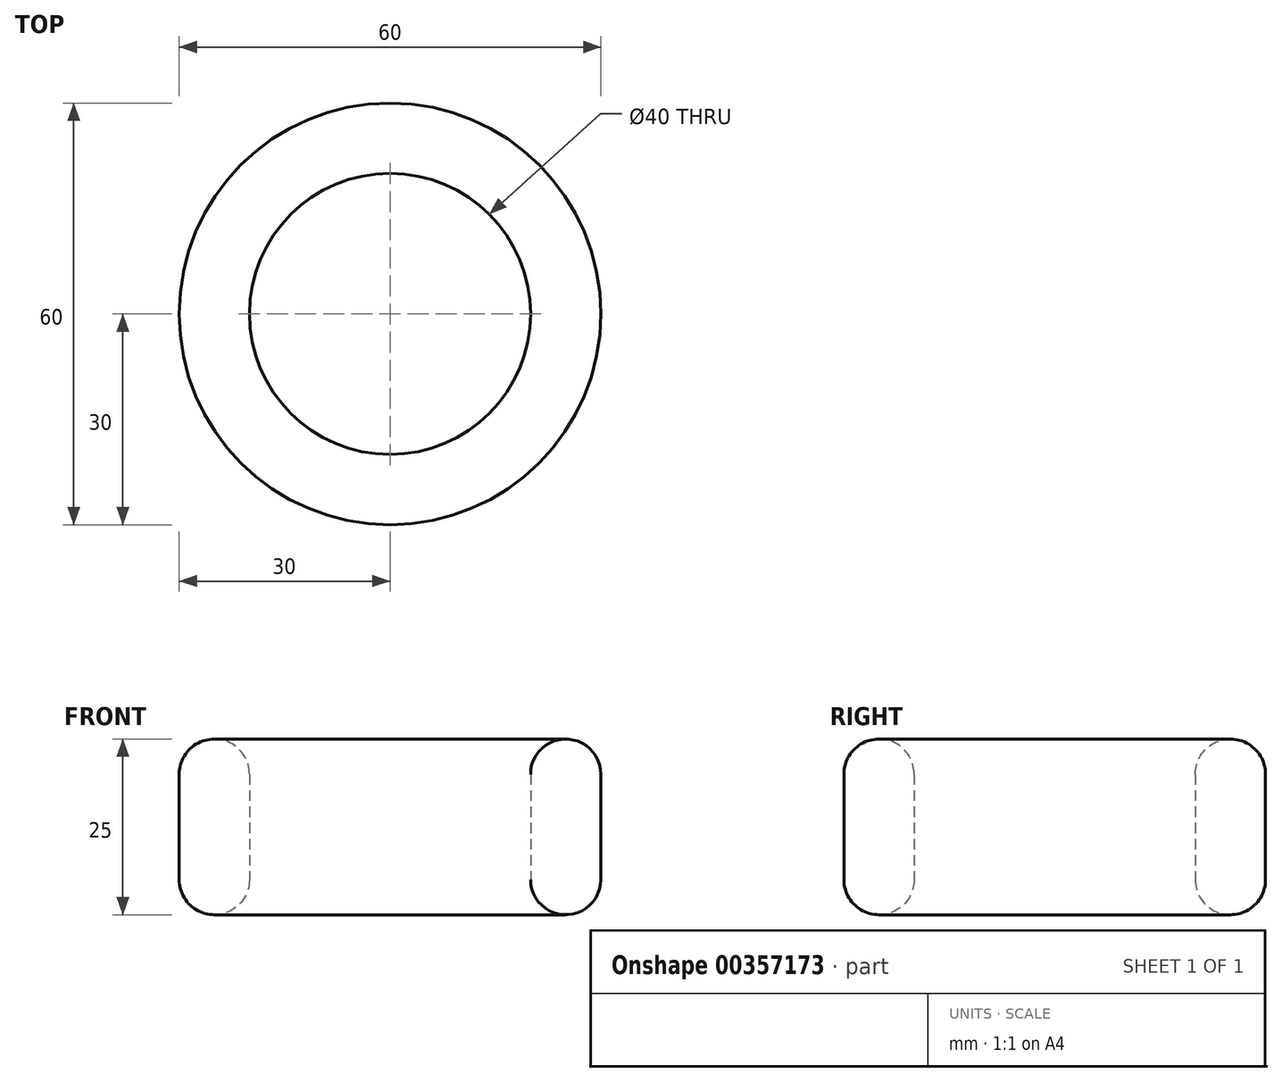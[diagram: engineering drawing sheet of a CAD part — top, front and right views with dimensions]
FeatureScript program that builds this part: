
annotation { "Feature Type Name" : "Feature", "Feature Type Description" : "" }
export const myFeature = defineFeature(function(context is Context, id is Id, definition is map)
    precondition{}
    {
        {
            var Q0;
            Q0=qCreatedBy(makeId("Top.planeOp"),FACE);
            var sketch = newSketch(context, id + "F0", { "sketchPlane" : qUnion([Q0])});
            skCircle(sketch, "E0", {"center": v(0, 0) * mm, "radius": 30 * mm});
            skCircle(sketch, "E1", {"center": v(0, 0) * mm, "radius": 20 * mm});
            skCircle(sketch, "E2", {"center": v(0, 0) * mm, "radius": 7.5 * mm});
            skSolve(sketch);
        }
        {
            var Q0;
            Q0 = qSketchRegion(id + "F0", true);
            extrude(context, id + "F1", {"entities" : qUnion([Q0]), "depth" : 25 * mm});
        }
        {
            var Q0;
            Q0=makeQuery(id+"F1.opExtrude","CAP_EDGE",EDGE,{"disambiguationData":[OSD([sQuery(id+"F0.wireOp",EDGE,"E0")])],"isStart":false});
            var Q1;
            Q1=makeQuery(id+"F1.opExtrude","CAP_FACE",FACE,{"disambiguationData":[OSD([sQuery(id+"F0.wireOp",EDGE,"E0"),sQuery(id+"F0.wireOp",EDGE,"E1")])],"isStart":false});
            var Q2;
            Q2=makeQuery(id+"F1.opExtrude","SWEPT_FACE",FACE,{"disambiguationData":[OSD([sQuery(id+"F0.wireOp",EDGE,"E0")])]});
            var Q3;
            Q3=makeQuery(id+"F1.opExtrude","CAP_FACE",FACE,{"disambiguationData":[OSD([sQuery(id+"F0.wireOp",EDGE,"E0"),sQuery(id+"F0.wireOp",EDGE,"E1")])],"isStart":true});
            fillet(context, id + "F2", {"entities" : qUnion([Q0, Q1, Q2, Q3]), "radius" : 5 * mm, "tangentPropagation" : true, "allowEdgeOverflow" : false});
        }
    });
